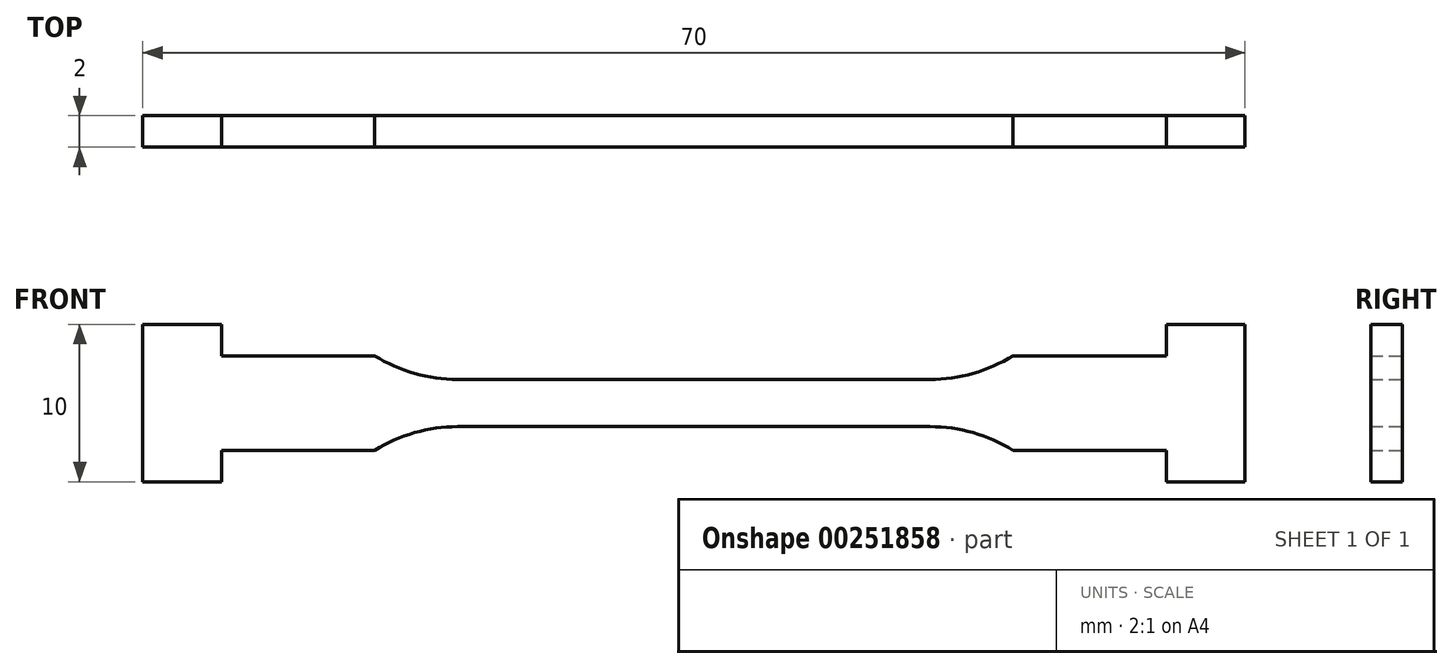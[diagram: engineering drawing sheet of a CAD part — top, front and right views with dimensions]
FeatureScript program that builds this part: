
annotation { "Feature Type Name" : "Feature", "Feature Type Description" : "" }
export const myFeature = defineFeature(function(context is Context, id is Id, definition is map)
    precondition{}
    {
        {
            var Q0;
            Q0=qCreatedBy(makeId("Front.planeOp"),FACE);
            var sketch = newSketch(context, id + "F0", { "sketchPlane" : qUnion([Q0])});
            skLineSegment(sketch, "E0.bottom", {"start": v(-35, 5) * mm, "end": v(-30, 5) * mm});
            skLineSegment(sketch, "E0.top", {"start": v(-35, -5) * mm, "end": v(-30, -5) * mm});
            skLineSegment(sketch, "E0.left", {"start": v(-35, 5) * mm, "end": v(-35, -5) * mm});
            skLineSegment(sketch, "E0.right", {"start": v(35, 5) * mm, "end": v(35, -5) * mm});
            skPoint(sketch, "E0.middle", {"position": v(0, 0) * mm});
            skLineSegment(sketch, "E1.bottom", {"start": v(-15, 1.5) * mm, "end": v(15, 1.5) * mm});
            skLineSegment(sketch, "E1.top", {"start": v(-15, -1.5) * mm, "end": v(15, -1.5) * mm});
            skLineSegment(sketch, "E1.left", {"start": v(-35, 1.5) * mm, "end": v(-35, -1.5) * mm});
            skLineSegment(sketch, "E1.right", {"start": v(35, 1.5) * mm, "end": v(35, -1.5) * mm});
            skLineSegment(sketch, "E2.bottom", {"start": v(35, 5) * mm, "end": v(30, 5) * mm});
            skLineSegment(sketch, "E2.top", {"start": v(35, -5) * mm, "end": v(30, -5) * mm});
            skLineSegment(sketch, "E2.right", {"start": v(30, 5) * mm, "end": v(30, 3) * mm});
            skLineSegment(sketch, "E3.right", {"start": v(-30, 5) * mm, "end": v(-30, 3) * mm});
            skLineSegment(sketch, "E4.bottom", {"start": v(-30, 3) * mm, "end": v(-20.27, 3) * mm});
            skLineSegment(sketch, "E4.top", {"start": v(-30, -3) * mm, "end": v(-20.27, -3) * mm});
            skPoint(sketch, "E4.middle", {"position": v(-22.5, 0) * mm});
            skLineSegment(sketch, "E5.bottom", {"start": v(30, 3) * mm, "end": v(20.27, 3) * mm});
            skLineSegment(sketch, "E5.top", {"start": v(30, -3) * mm, "end": v(20.27, -3) * mm});
            skPoint(sketch, "E5.middle", {"position": v(22.5, 0) * mm});
            skArc(sketch, "E6", {"start": v(-20.27, 3) * mm, "mid": v(-17.74, 1.88) * mm, "end": v(-15, 1.5) * mm});
            skArc(sketch, "E7", {"start": v(15, 1.5) * mm, "mid": v(17.74, 1.88) * mm, "end": v(20.27, 3) * mm});
            skArc(sketch, "E8", {"start": v(-15, -1.5) * mm, "mid": v(-17.74, -1.88) * mm, "end": v(-20.27, -3) * mm});
            skArc(sketch, "E9", {"start": v(20.27, -3) * mm, "mid": v(17.74, -1.88) * mm, "end": v(15, -1.5) * mm});
            skLineSegment(sketch, "E10.trimOffspring", {"start": v(30, 5) * mm, "end": v(35, 5) * mm});
            skPoint(sketch, "E11.orphan", {"position": v(-15, 3) * mm});
            skPoint(sketch, "E12.orphan", {"position": v(15, 3) * mm});
            skLineSegment(sketch, "E13.trimOffspring", {"start": v(30, -5) * mm, "end": v(35, -5) * mm});
            skPoint(sketch, "E14.end.orphan", {"position": v(15, -3) * mm});
            skPoint(sketch, "E15.end.orphan", {"position": v(-15, -3) * mm});
            skLineSegment(sketch, "E16.trimOffspring", {"start": v(-30, -3) * mm, "end": v(-30, -5) * mm});
            skLineSegment(sketch, "E17.trimOffspring", {"start": v(30, -3) * mm, "end": v(30, -5) * mm});
            skSolve(sketch);
        }
        {
            var Q0;
            Q0=makeQuery(id+"F0.imprint","IMPRINT",FACE,{"disambiguationData":[TD([[makeQuery(id+"F0.imprint","IMPRINT",EDGE,{"derivedFrom":sQuery(id+"F0.wireOp",EDGE,"E1.bottom")}),-1.0]])]});
            extrude(context, id + "F1", {"entities" : qUnion([Q0]), "depth" : 2 * mm});
        }
    });
